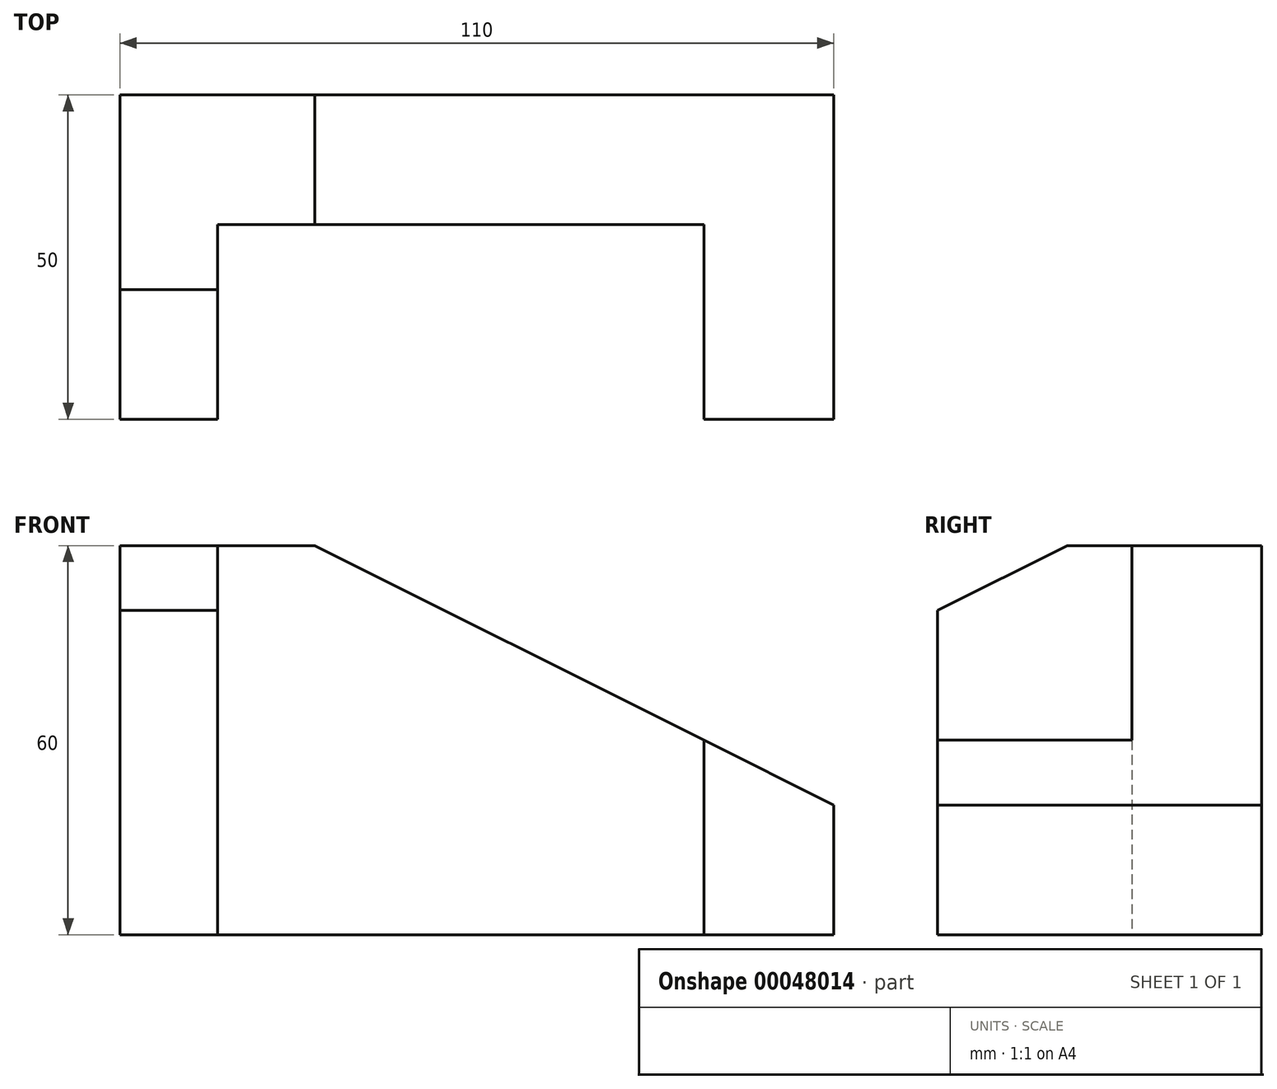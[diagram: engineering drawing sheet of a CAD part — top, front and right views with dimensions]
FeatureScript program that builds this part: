
annotation { "Feature Type Name" : "Feature", "Feature Type Description" : "" }
export const myFeature = defineFeature(function(context is Context, id is Id, definition is map)
    precondition{}
    {
        {
            var Q0;
            Q0=qCreatedBy(makeId("Front.planeOp"),FACE);
            var sketch = newSketch(context, id + "F0", { "sketchPlane" : qUnion([Q0])});
            skLineSegment(sketch, "E0", {"start": v(0, 0) * mm, "end": v(0, 60) * mm});
            skLineSegment(sketch, "E1", {"start": v(0, 60) * mm, "end": v(30, 60) * mm});
            skLineSegment(sketch, "E2", {"start": v(30, 60) * mm, "end": v(110, 20) * mm});
            skLineSegment(sketch, "E3", {"start": v(110, 20) * mm, "end": v(110, 0) * mm});
            skLineSegment(sketch, "E4", {"start": v(110, 0) * mm, "end": v(0, 0) * mm});
            skLineSegment(sketch, "E5", {"start": v(15, 60) * mm, "end": v(15, 0) * mm});
            skLineSegment(sketch, "E6", {"start": v(90, 30) * mm, "end": v(90, 0) * mm});
            skSolve(sketch);
        }
        {
            var Q0;
            Q0 = qSketchRegion(id + "F0", true);
            extrude(context, id + "F1", {"entities" : qUnion([Q0]), "oppositeDirection" : true, "depth" : 50 * mm});
        }
        {
            var Q0;
            {var subQ5=sQuery(id+"F0.wireOp",EDGE,"E5");Q0=makeQuery(id+"F0.imprint","IMPRINT",FACE,{"disambiguationData":[TD([[makeQuery(id+"F0.imprint","IMPRINT",EDGE,{"derivedFrom":subQ5}),1.0]])]});}
            extrude(context, id + "F2", {"entities" : qUnion([Q0]), "operationType" : NewBodyOperationType.REMOVE, "oppositeDirection" : true, "depth" : 30 * mm});
        }
        {
            var Q0;
            Q0=makeQuery(id+"F1.opExtrude","CAP_EDGE",EDGE,{"disambiguationData":[OSD([sQuery(id+"F0.wireOp",EDGE,"E1")])],"isStart":true});
            chamfer(context, id + "F3", {"entities" : qUnion([Q0]), "chamferType" : ChamferType.TWO_OFFSETS, "width1" : 20 * mm, "oppositeDirection" : false, "width2" : 10 * mm, "tangentPropagation" : true});
        }
    });
